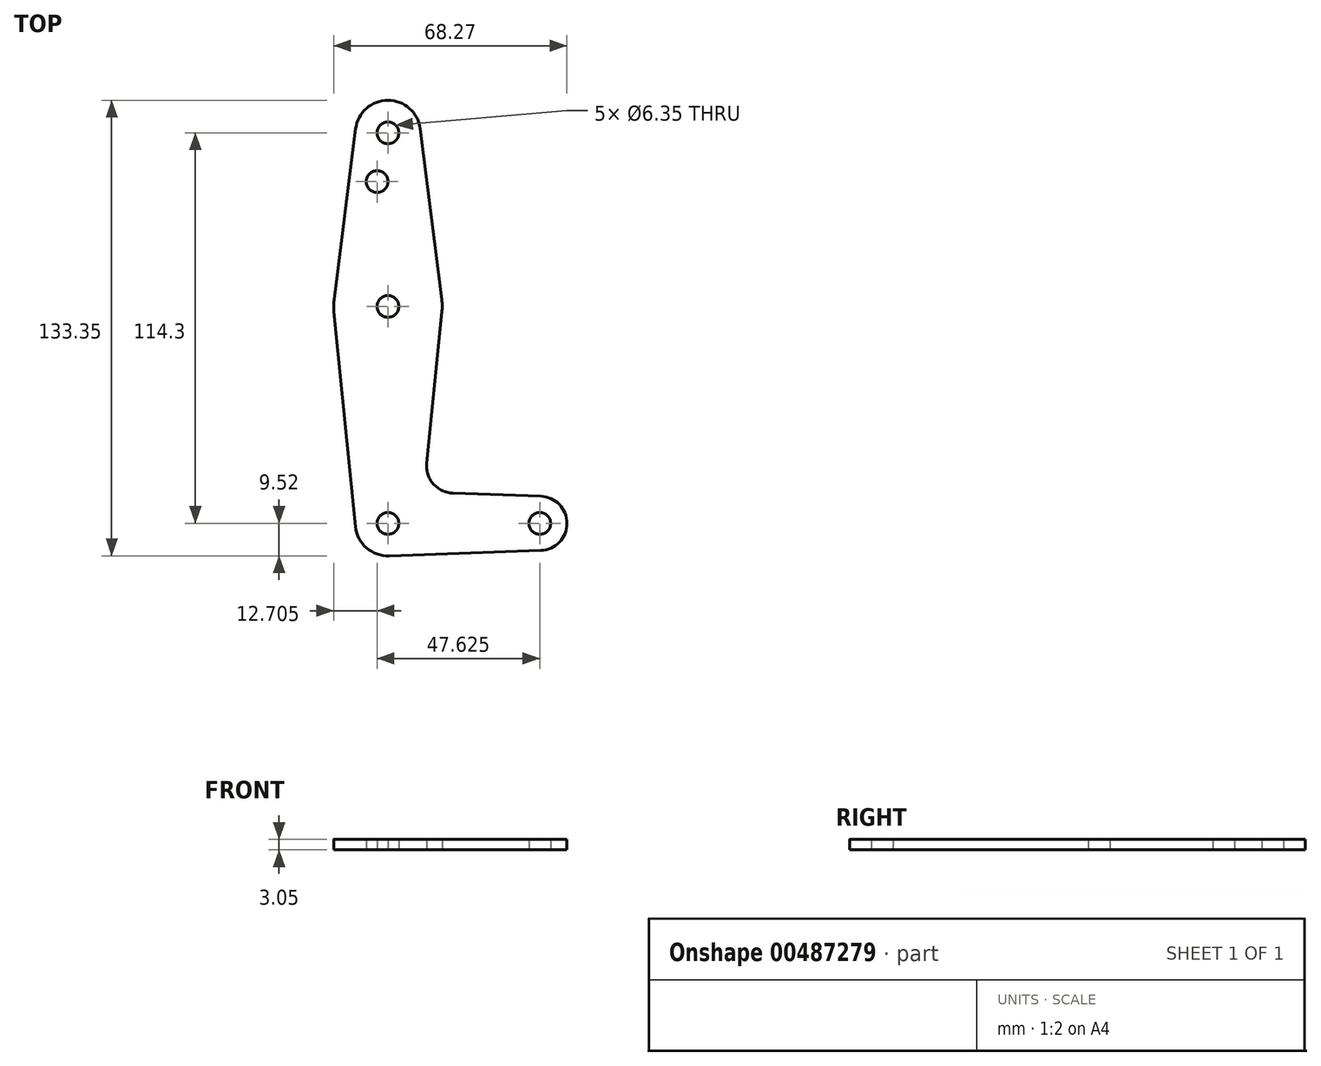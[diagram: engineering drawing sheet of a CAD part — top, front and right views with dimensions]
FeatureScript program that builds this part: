
annotation { "Feature Type Name" : "Feature", "Feature Type Description" : "" }
export const myFeature = defineFeature(function(context is Context, id is Id, definition is map)
    precondition{}
    {
        {
            var Q0;
            Q0=qCreatedBy(makeId("Top.planeOp"),FACE);
            var sketch = newSketch(context, id + "F0", { "sketchPlane" : qUnion([Q0])});
            skLineSegment(sketch, "E0", {"start": v(0, 0) * mm, "end": v(0, 114.3) * mm, "construction": true});
            skLineSegment(sketch, "E1", {"start": v(0, 0) * mm, "end": v(44.45, 0) * mm, "construction": true});
            skCircle(sketch, "E2", {"center": v(0, 114.3) * mm, "radius": 9.53 * mm});
            skCircle(sketch, "E3", {"center": v(44.45, 0) * mm, "radius": 7.94 * mm});
            skCircle(sketch, "E4", {"center": v(0, 0) * mm, "radius": 9.53 * mm});
            skCircle(sketch, "E5", {"center": v(0, 63.5) * mm, "radius": 15.88 * mm});
            skLineSegment(sketch, "E6", {"start": v(9.45, 115.5) * mm, "end": v(15.75, 65.48) * mm});
            skLineSegment(sketch, "E7", {"start": v(-9.45, 115.5) * mm, "end": v(-15.75, 65.48) * mm});
            skLineSegment(sketch, "E8", {"start": v(15.8, 61.91) * mm, "end": v(11.34, 17.6) * mm});
            skLineSegment(sketch, "E9", {"start": v(-15.8, 61.91) * mm, "end": v(-9.48, -0.95) * mm});
            skLineSegment(sketch, "E10", {"start": v(0.34, -9.52) * mm, "end": v(44.73, -7.93) * mm});
            skLineSegment(sketch, "E11", {"start": v(18.97, 8.85) * mm, "end": v(44.73, 7.93) * mm});
            skCircle(sketch, "E12", {"center": v(0, 114.3) * mm, "radius": 3.18 * mm});
            skCircle(sketch, "E13", {"center": v(0, 63.5) * mm, "radius": 3.18 * mm});
            skCircle(sketch, "E14", {"center": v(0, 0) * mm, "radius": 3.18 * mm});
            skCircle(sketch, "E15", {"center": v(44.45, 0) * mm, "radius": 3.18 * mm});
            skCircle(sketch, "E16", {"center": v(-3.18, 100.03) * mm, "radius": 3.18 * mm});
            skArc(sketch, "E17.filletArc", {"start": v(11.34, 17.6) * mm, "mid": v(13.26, 11.57) * mm, "end": v(18.97, 8.85) * mm});
            skSolve(sketch);
        }
        {
            var Q0;
            Q0 = qSketchRegion(id + "F0", true);
            extrude(context, id + "F1", {"entities" : qUnion([Q0]), "depth" : 3.05 * mm});
        }
    });
